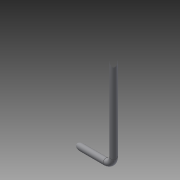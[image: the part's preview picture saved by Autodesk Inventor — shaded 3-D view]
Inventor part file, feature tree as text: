
AUTODESK INVENTOR PART (.ipt)
format: ipt  version: 2014 SP1 (Build 180222100, 222)  size: 77,312 bytes
history: native  units: in
note: dims shown in document units (in); Inventor stores cm internally (conversion verified against a paired STEP export)
features: sketch x2, sweep x1
ambient origin geometry x8: Origin, YZ Plane, XZ Plane, XY Plane, X Axis, Y Axis, Z Axis, Center Point
bodies: Solid1 (feature_tree)
feature tree (3):
  sweep  "Sweep1"
  sketch  "Sketch1"  dims[d3=0.3in d4=0.0in]
  sketch  "Sketch2"  dims[d5=5.5in d6=0.375in]
